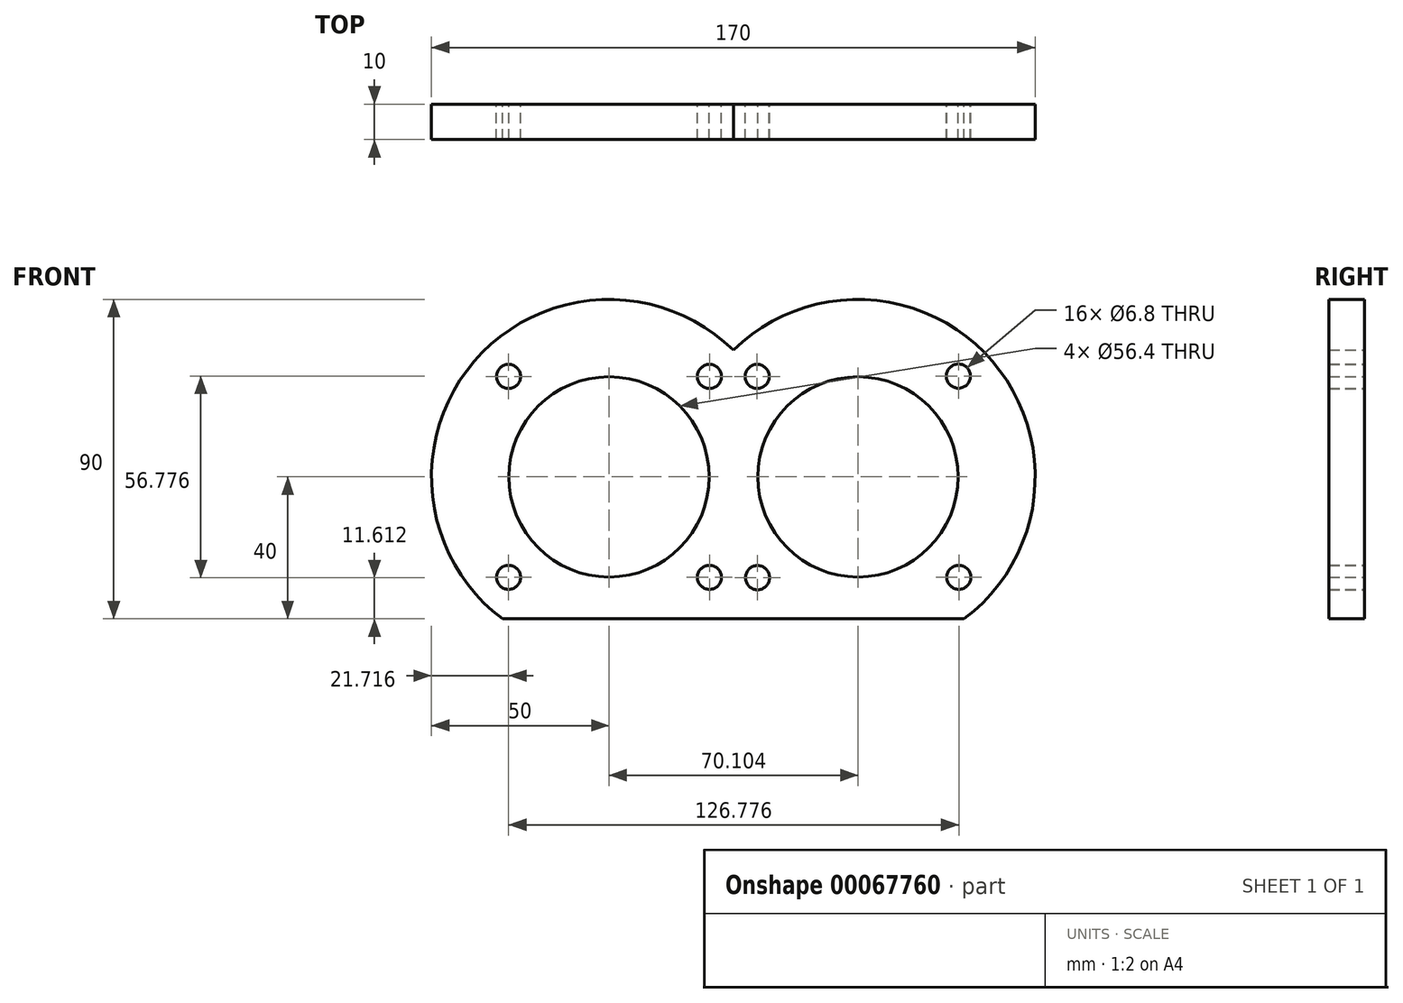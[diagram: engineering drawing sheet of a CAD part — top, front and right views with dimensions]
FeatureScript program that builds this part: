
annotation { "Feature Type Name" : "Feature", "Feature Type Description" : "" }
export const myFeature = defineFeature(function(context is Context, id is Id, definition is map)
    precondition{}
    {
        {
            var Q0;
            Q0=qCreatedBy(makeId("Front.planeOp"),FACE);
            var sketch = newSketch(context, id + "F0", { "sketchPlane" : qUnion([Q0])});
            skCircle(sketch, "E0", {"center": v(-35, 0) * mm, "radius": 28.2 * mm});
            skArc(sketch, "E1", {"start": v(0, 35.7) * mm, "mid": v(-72.94, 32.57) * mm, "end": v(-65, -40) * mm});
            skArc(sketch, "E2.trimOffspring", {"start": v(65, -40) * mm, "mid": v(72.94, 32.57) * mm, "end": v(0, 35.7) * mm});
            skCircle(sketch, "E3", {"center": v(35.1, 0) * mm, "radius": 28.2 * mm});
            skCircle(sketch, "E4.1.0", {"center": v(-63.28, 28.28) * mm, "radius": 3.4 * mm});
            skCircle(sketch, "E4.3.0", {"center": v(-63.28, -28.28) * mm, "radius": 3.4 * mm});
            skCircle(sketch, "E4.5.0", {"center": v(-6.72, -28.28) * mm, "radius": 3.4 * mm});
            skCircle(sketch, "E4.7.0", {"center": v(-6.72, 28.28) * mm, "radius": 3.4 * mm});
            skCircle(sketch, "E5.1.0", {"center": v(6.72, 28.28) * mm, "radius": 3.4 * mm});
            skCircle(sketch, "E6.1.3.0", {"center": v(6.82, -28.39) * mm, "radius": 3.4 * mm});
            skCircle(sketch, "E6.1.5.0", {"center": v(63.5, -28.28) * mm, "radius": 3.4 * mm});
            skCircle(sketch, "E6.1.7.0", {"center": v(63.39, 28.39) * mm, "radius": 3.4 * mm});
            skLineSegment(sketch, "E7.0", {"start": v(-65, -40) * mm, "end": v(65, -40) * mm});
            skCircle(sketch, "E8", {"center": v(35.1, 0) * mm, "radius": 40.07 * mm, "construction": true});
            skSolve(sketch);
        }
        {
            var Q0;
            Q0=makeQuery(id+"F0.imprint","IMPRINT",FACE,{"disambiguationData":[TD([[makeQuery(id+"F0.imprint","IMPRINT",EDGE,{"derivedFrom":sQuery(id+"F0.wireOp",EDGE,"E0")}),-1.0]])]});
            var Q1;
            Q1=makeQuery(id+"F0.imprint","IMPRINT",FACE,{"disambiguationData":[TD([[makeQuery(id+"F0.imprint","IMPRINT",EDGE,{"derivedFrom":sQuery(id+"F0.wireOp",EDGE,"E2.trimOffspring")}),1.0]])]});
            extrude(context, id + "F1", {"entities" : qUnion([Q0, Q1]), "depth" : 10 * mm});
        }
    });
